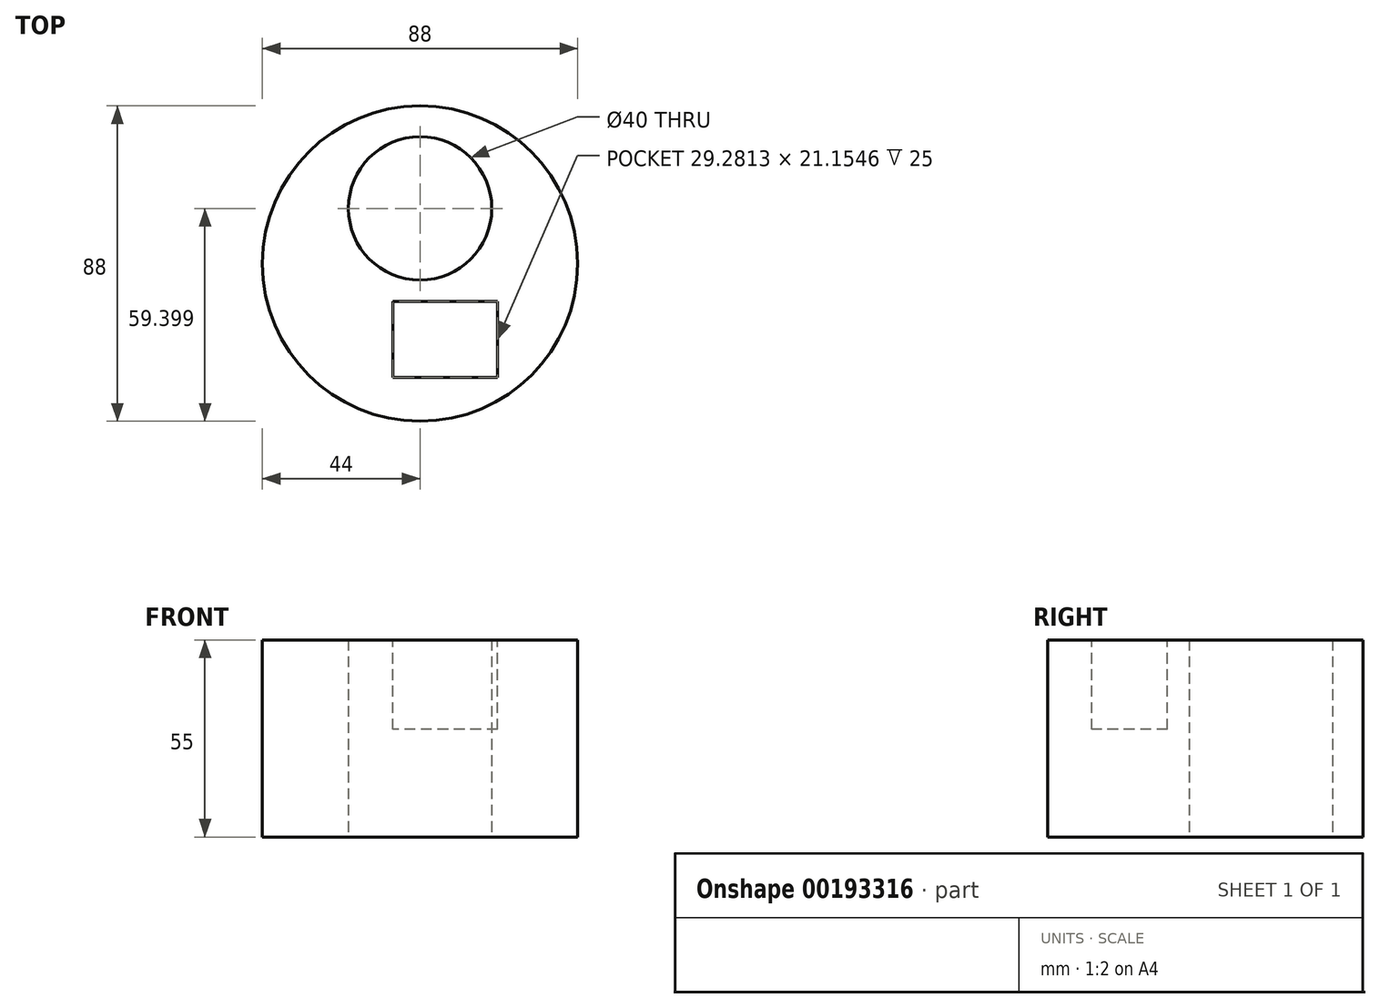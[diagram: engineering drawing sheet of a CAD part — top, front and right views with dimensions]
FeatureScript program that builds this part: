
annotation { "Feature Type Name" : "Feature", "Feature Type Description" : "" }
export const myFeature = defineFeature(function(context is Context, id is Id, definition is map)
    precondition{}
    {
        {
            var Q0;
            Q0=qCreatedBy(makeId("Front.planeOp"),FACE);
            var sketch = newSketch(context, id + "F0", { "sketchPlane" : qUnion([Q0])});
            skLineSegment(sketch, "E0.bottom", {"start": v(-44, 55) * mm, "end": v(0, 55) * mm});
            skLineSegment(sketch, "E0.top", {"start": v(-44, 0) * mm, "end": v(0, 0) * mm});
            skLineSegment(sketch, "E0.left", {"start": v(-44, 55) * mm, "end": v(-44, 0) * mm});
            skLineSegment(sketch, "E0.right", {"start": v(0, 55) * mm, "end": v(0, 0) * mm});
            skSolve(sketch);
        }
        {
            var Q0;
            Q0=makeQuery(id+"F0.imprint","IMPRINT",FACE,{"disambiguationData":[TD([[makeQuery(id+"F0.imprint","IMPRINT",EDGE,{"derivedFrom":sQuery(id+"F0.wireOp",EDGE,"E0.bottom")}),-1.0]])]});
            var Q1;
            Q1=sQuery(id+"F0.wireOp",EDGE,"E0.right");
            revolve(context, id + "F1", {"entities" : qUnion([Q0]), "axis" : qUnion([Q1]), "revolveType" : RevolveType.FULL});
        }
        {
            var Q0;
            Q0=makeQuery(id+"F1.opRevolve","SWEPT_FACE",FACE,{"disambiguationData":[OSD([sQuery(id+"F0.wireOp",EDGE,"E0.top")])]});
            var sketch = newSketch(context, id + "F2", { "sketchPlane" : qUnion([Q0])});
            skCircle(sketch, "E1", {"center": v(0, -15.4) * mm, "radius": 20 * mm});
            skSolve(sketch);
        }
        {
            var Q0;
            Q0=makeQuery(id+"F2.imprint","IMPRINT",FACE,{"disambiguationData":[TD([[makeQuery(id+"F2.imprint","IMPRINT",EDGE,{"derivedFrom":sQuery(id+"F2.wireOp",EDGE,"E1")}),1.0]])]});
            extrude(context, id + "F3", {"entities" : qUnion([Q0]), "operationType" : NewBodyOperationType.REMOVE, "oppositeDirection" : true, "depth" : 133.83 * mm});
        }
        {
            var Q0;
            Q0=makeQuery(id+"F1.opRevolve","SWEPT_FACE",FACE,{"disambiguationData":[OSD([sQuery(id+"F0.wireOp",EDGE,"E0.bottom")])]});
            var sketch = newSketch(context, id + "F4", { "sketchPlane" : qUnion([Q0])});
            skLineSegment(sketch, "E2.bottom", {"start": v(21.64, -10.6) * mm, "end": v(-7.64, -10.6) * mm});
            skLineSegment(sketch, "E2.top", {"start": v(21.64, -31.75) * mm, "end": v(-7.64, -31.75) * mm});
            skLineSegment(sketch, "E2.left", {"start": v(21.64, -10.6) * mm, "end": v(21.64, -31.75) * mm});
            skLineSegment(sketch, "E2.right", {"start": v(-7.64, -10.6) * mm, "end": v(-7.64, -31.75) * mm});
            skSolve(sketch);
        }
        {
            var Q0;
            Q0 = qSketchRegion(id + "F4", true);
            extrude(context, id + "F5", {"entities" : qUnion([Q0]), "operationType" : NewBodyOperationType.REMOVE, "oppositeDirection" : true, "depth" : 25 * mm});
        }
    });
